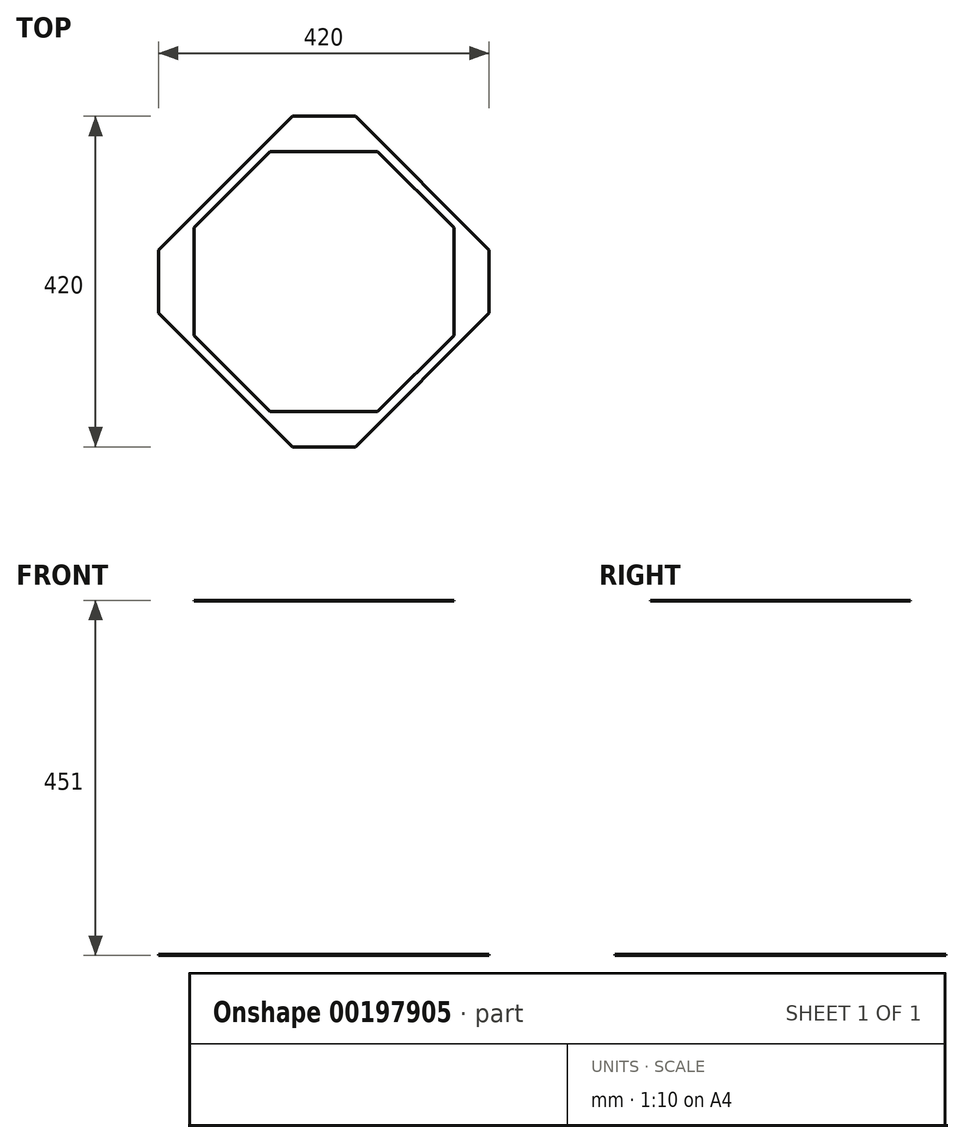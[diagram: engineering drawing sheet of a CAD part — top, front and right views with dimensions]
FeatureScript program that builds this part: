
annotation { "Feature Type Name" : "Feature", "Feature Type Description" : "" }
export const myFeature = defineFeature(function(context is Context, id is Id, definition is map)
    precondition{}
    {
        {
            var Q0;
            Q0=qCreatedBy(makeId("Top.planeOp"),FACE);
            cPlane(context, id + "F0", {"entities" : qUnion([Q0]), "cplaneType" : CPlaneType.OFFSET, "offset" : 450 * mm, "width" : 150 * mm, "height" : 150 * mm});
        }
        {
            var Q0;
            Q0=qCreatedBy(id+"F0.planeOp",FACE);
            var sketch = newSketch(context, id + "F1", { "sketchPlane" : qUnion([Q0])});
            skLineSegment(sketch, "E0", {"start": v(-268.04, 0) * mm, "end": v(272.69, 0) * mm, "construction": true});
            skLineSegment(sketch, "E1", {"start": v(0, -270.5) * mm, "end": v(0, 286.74) * mm, "construction": true});
            skLineSegment(sketch, "E2.0", {"start": v(165, 68.35) * mm, "end": v(165, -68.35) * mm});
            skLineSegment(sketch, "E2.1", {"start": v(165, -68.35) * mm, "end": v(68.35, -165) * mm});
            skLineSegment(sketch, "E2.2", {"start": v(68.35, -165) * mm, "end": v(-68.35, -165) * mm});
            skLineSegment(sketch, "E2.3", {"start": v(-68.35, -165) * mm, "end": v(-165, -68.35) * mm});
            skLineSegment(sketch, "E2.4", {"start": v(-165, -68.35) * mm, "end": v(-165, 68.35) * mm});
            skLineSegment(sketch, "E2.5", {"start": v(-165, 68.35) * mm, "end": v(-68.35, 165) * mm});
            skLineSegment(sketch, "E2.6", {"start": v(-68.35, 165) * mm, "end": v(68.35, 165) * mm});
            skLineSegment(sketch, "E2.7", {"start": v(68.35, 165) * mm, "end": v(165, 68.35) * mm});
            skPoint(sketch, "E2.0.midPoint", {"position": v(165, 0) * mm});
            skSolve(sketch);
        }
        {
            var Q0;
            Q0=qCreatedBy(makeId("Top.planeOp"),FACE);
            var sketch = newSketch(context, id + "F2", { "sketchPlane" : qUnion([Q0])});
            skLineSegment(sketch, "E3.1", {"start": v(-210, -40) * mm, "end": v(-210, 40) * mm});
            skLineSegment(sketch, "E3.2", {"start": v(-40, 210) * mm, "end": v(40, 210) * mm});
            skLineSegment(sketch, "E3.5", {"start": v(210, 40) * mm, "end": v(210, -40) * mm});
            skLineSegment(sketch, "E3.7", {"start": v(40, -210) * mm, "end": v(-40, -210) * mm});
            skSolve(sketch);
        }
        {
            var Q0;
            Q0=sQuery(id+"F2.wireOp",VERTEX,"E3.5.end");
            var Q1;
            Q1=sQuery(id+"F2.wireOp",VERTEX,"E3.5.start");
            var Q2;
            Q2=sQuery(id+"F1.wireOp",VERTEX,"E2.1.start");
            cPlane(context, id + "F3", {"entities" : qUnion([Q0, Q1, Q2]), "cplaneType" : CPlaneType.THREE_POINT, "offset" : 25 * mm, "width" : 150 * mm, "height" : 150 * mm});
        }
        {
            var Q0;
            Q0=sQuery(id+"F2.wireOp",VERTEX,"E3.5.end");
            var Q1;
            Q1=sQuery(id+"F1.wireOp",VERTEX,"E2.2.start");
            var Q2;
            Q2=sQuery(id+"F1.wireOp",VERTEX,"E2.0.end");
            cPlane(context, id + "F4", {"entities" : qUnion([Q0, Q1, Q2]), "cplaneType" : CPlaneType.THREE_POINT, "offset" : 25 * mm, "width" : 150 * mm, "height" : 150 * mm});
        }
        {
            var Q0;
            Q0=sQuery(id+"F2.wireOp",VERTEX,"E3.7.end");
            var Q1;
            Q1=sQuery(id+"F2.wireOp",VERTEX,"E3.7.start");
            var Q2;
            Q2=sQuery(id+"F1.wireOp",VERTEX,"E2.3.start");
            cPlane(context, id + "F5", {"entities" : qUnion([Q0, Q1, Q2]), "cplaneType" : CPlaneType.THREE_POINT, "offset" : 25 * mm, "width" : 150 * mm, "height" : 150 * mm});
        }
        {
            var Q0;
            Q0=sQuery(id+"F1.wireOp",VERTEX,"E2.3.start");
            var Q1;
            Q1=sQuery(id+"F1.wireOp",VERTEX,"E2.4.start");
            var Q2;
            Q2=sQuery(id+"F2.wireOp",VERTEX,"E3.7.end");
            cPlane(context, id + "F6", {"entities" : qUnion([Q0, Q1, Q2]), "cplaneType" : CPlaneType.THREE_POINT, "offset" : 25 * mm, "width" : 150 * mm, "height" : 150 * mm});
        }
        {
            var Q0;
            Q0=sQuery(id+"F2.wireOp",VERTEX,"E3.1.end");
            var Q1;
            Q1=sQuery(id+"F2.wireOp",VERTEX,"E3.1.start");
            var Q2;
            Q2=sQuery(id+"F1.wireOp",VERTEX,"E2.5.start");
            cPlane(context, id + "F7", {"entities" : qUnion([Q0, Q1, Q2]), "cplaneType" : CPlaneType.THREE_POINT, "offset" : 25 * mm, "width" : 150 * mm, "height" : 150 * mm});
        }
        {
            var Q0;
            Q0=sQuery(id+"F1.wireOp",VERTEX,"E2.6.start");
            var Q1;
            Q1=sQuery(id+"F1.wireOp",VERTEX,"E2.5.start");
            var Q2;
            Q2=sQuery(id+"F2.wireOp",VERTEX,"E3.2.start");
            cPlane(context, id + "F8", {"entities" : qUnion([Q0, Q1, Q2]), "cplaneType" : CPlaneType.THREE_POINT, "offset" : 25 * mm, "width" : 150 * mm, "height" : 150 * mm});
        }
        {
            var Q0;
            Q0=sQuery(id+"F2.wireOp",VERTEX,"E3.2.end");
            var Q1;
            Q1=sQuery(id+"F2.wireOp",VERTEX,"E3.2.start");
            var Q2;
            Q2=sQuery(id+"F1.wireOp",VERTEX,"E2.6.end");
            cPlane(context, id + "F9", {"entities" : qUnion([Q0, Q1, Q2]), "cplaneType" : CPlaneType.THREE_POINT, "offset" : 25 * mm, "width" : 150 * mm, "height" : 150 * mm});
        }
        {
            var Q0;
            Q0=sQuery(id+"F1.wireOp",VERTEX,"E2.7.end");
            var Q1;
            Q1=sQuery(id+"F1.wireOp",VERTEX,"E2.6.end");
            var Q2;
            Q2=sQuery(id+"F2.wireOp",VERTEX,"E3.5.start");
            cPlane(context, id + "F10", {"entities" : qUnion([Q0, Q1, Q2]), "cplaneType" : CPlaneType.THREE_POINT, "offset" : 25 * mm, "width" : 150 * mm, "height" : 150 * mm});
        }
        {
            var Q0;
            Q0=qCreatedBy(id+"F3.planeOp",FACE);
            var sketch = newSketch(context, id + "F11", { "sketchPlane" : qUnion([Q0])});
            skPoint(sketch, "E4.0", {"position": v(40, -20.9) * mm});
            skPoint(sketch, "E4.1", {"position": v(-40, -20.9) * mm});
            skPoint(sketch, "E5.0", {"position": v(68.35, 431.35) * mm});
            skPoint(sketch, "E6.0", {"position": v(-68.35, 431.35) * mm});
            skLineSegment(sketch, "E7", {"start": v(40, -20.9) * mm, "end": v(68.35, 431.35) * mm});
            skLineSegment(sketch, "E8", {"start": v(-68.35, 431.35) * mm, "end": v(-40, -20.9) * mm});
            skLineSegment(sketch, "E9", {"start": v(68.35, 431.35) * mm, "end": v(-40, -20.9) * mm});
            skLineSegment(sketch, "E10", {"start": v(40, -20.9) * mm, "end": v(-68.35, 431.35) * mm});
            skSolve(sketch);
        }
        {
            var Q0;
            Q0=qCreatedBy(id+"F4.planeOp",FACE);
            var sketch = newSketch(context, id + "F12", { "sketchPlane" : qUnion([Q0])});
            skPoint(sketch, "E11.0", {"position": v(-56.67, 447.16) * mm});
            skPoint(sketch, "E12.0", {"position": v(79.97, 443.59) * mm});
            skPoint(sketch, "E13.0", {"position": v(-120.29, -1.48) * mm});
            skPoint(sketch, "E14.0", {"position": v(120.05, -7.77) * mm});
            skLineSegment(sketch, "E15", {"start": v(120.05, -7.77) * mm, "end": v(-56.67, 447.16) * mm});
            skLineSegment(sketch, "E16", {"start": v(-120.29, -1.48) * mm, "end": v(79.97, 443.59) * mm});
            skSolve(sketch);
        }
        {
            var Q0;
            Q0=qCreatedBy(id+"F5.planeOp",FACE);
            var sketch = newSketch(context, id + "F13", { "sketchPlane" : qUnion([Q0])});
            skPoint(sketch, "E17.0", {"position": v(68.35, 431.35) * mm});
            skPoint(sketch, "E18.0", {"position": v(-68.35, 431.35) * mm});
            skPoint(sketch, "E19.0", {"position": v(40, -20.9) * mm});
            skPoint(sketch, "E20.0", {"position": v(-40, -20.9) * mm});
            skLineSegment(sketch, "E21", {"start": v(68.35, 431.35) * mm, "end": v(40, -20.9) * mm});
            skLineSegment(sketch, "E22", {"start": v(40, -20.9) * mm, "end": v(-68.35, 431.35) * mm});
            skLineSegment(sketch, "E23", {"start": v(-68.35, 431.35) * mm, "end": v(-40, -20.9) * mm});
            skLineSegment(sketch, "E24", {"start": v(-40, -20.9) * mm, "end": v(68.35, 431.35) * mm});
            skSolve(sketch);
        }
        {
            var Q0;
            Q0=qCreatedBy(id+"F6.planeOp",FACE);
            var sketch = newSketch(context, id + "F14", { "sketchPlane" : qUnion([Q0])});
            skPoint(sketch, "E25.0", {"position": v(79.97, 443.59) * mm});
            skPoint(sketch, "E26.0", {"position": v(-56.67, 447.16) * mm});
            skPoint(sketch, "E27.0", {"position": v(120.05, -7.77) * mm});
            skPoint(sketch, "E28.0", {"position": v(-120.29, -1.48) * mm});
            skLineSegment(sketch, "E29", {"start": v(79.97, 443.59) * mm, "end": v(-120.29, -1.48) * mm});
            skLineSegment(sketch, "E30", {"start": v(120.05, -7.77) * mm, "end": v(-56.67, 447.16) * mm});
            skSolve(sketch);
        }
        {
            var Q0;
            Q0=qCreatedBy(id+"F7.planeOp",FACE);
            var sketch = newSketch(context, id + "F15", { "sketchPlane" : qUnion([Q0])});
            skPoint(sketch, "E31.0", {"position": v(68.35, 431.35) * mm});
            skPoint(sketch, "E32.0", {"position": v(-68.35, 431.35) * mm});
            skPoint(sketch, "E33.0", {"position": v(40, -20.9) * mm});
            skPoint(sketch, "E34.0", {"position": v(-40, -20.9) * mm});
            skLineSegment(sketch, "E35", {"start": v(68.35, 431.35) * mm, "end": v(40, -20.9) * mm});
            skLineSegment(sketch, "E36", {"start": v(-68.35, 431.35) * mm, "end": v(40, -20.9) * mm});
            skLineSegment(sketch, "E37", {"start": v(-40, -20.9) * mm, "end": v(68.35, 431.35) * mm});
            skLineSegment(sketch, "E38", {"start": v(-68.35, 431.35) * mm, "end": v(-40, -20.9) * mm});
            skSolve(sketch);
        }
        {
            var Q0;
            Q0=qCreatedBy(id+"F8.planeOp",FACE);
            var sketch = newSketch(context, id + "F16", { "sketchPlane" : qUnion([Q0])});
            skPoint(sketch, "E39.0", {"position": v(-79.97, 443.59) * mm});
            skPoint(sketch, "E40.0", {"position": v(56.67, 447.16) * mm});
            skPoint(sketch, "E41.0", {"position": v(-120.05, -7.77) * mm});
            skPoint(sketch, "E42.0", {"position": v(120.29, -1.48) * mm});
            skLineSegment(sketch, "E43", {"start": v(-120.05, -7.77) * mm, "end": v(56.67, 447.16) * mm});
            skLineSegment(sketch, "E44", {"start": v(-79.97, 443.59) * mm, "end": v(120.29, -1.48) * mm});
            skSolve(sketch);
        }
        {
            var Q0;
            Q0=qCreatedBy(id+"F9.planeOp",FACE);
            var sketch = newSketch(context, id + "F17", { "sketchPlane" : qUnion([Q0])});
            skPoint(sketch, "E45.0", {"position": v(68.35, 431.35) * mm});
            skPoint(sketch, "E46.0", {"position": v(-68.35, 431.35) * mm});
            skPoint(sketch, "E47.0", {"position": v(40, -20.9) * mm});
            skPoint(sketch, "E48.0", {"position": v(-40, -20.9) * mm});
            skLineSegment(sketch, "E49", {"start": v(68.35, 431.35) * mm, "end": v(40, -20.9) * mm});
            skLineSegment(sketch, "E50", {"start": v(40, -20.9) * mm, "end": v(-68.35, 431.35) * mm});
            skLineSegment(sketch, "E51", {"start": v(-68.35, 431.35) * mm, "end": v(-40, -20.9) * mm});
            skLineSegment(sketch, "E52", {"start": v(-40, -20.9) * mm, "end": v(68.35, 431.35) * mm});
            skSolve(sketch);
        }
        {
            var Q0;
            Q0=qCreatedBy(id+"F0.planeOp",FACE);
            var sketch = newSketch(context, id + "F18", { "sketchPlane" : qUnion([Q0])});
            skLineSegment(sketch, "E53.0.0", {"start": v(165, 68.35) * mm, "end": v(68.35, 165) * mm});
            skLineSegment(sketch, "E53.0.1", {"start": v(68.35, 165) * mm, "end": v(-68.35, 165) * mm});
            skLineSegment(sketch, "E53.0.2", {"start": v(-68.35, 165) * mm, "end": v(-165, 68.35) * mm});
            skLineSegment(sketch, "E53.0.3", {"start": v(-165, 68.35) * mm, "end": v(-165, -68.35) * mm});
            skLineSegment(sketch, "E53.0.4", {"start": v(-165, -68.35) * mm, "end": v(-68.35, -165) * mm});
            skLineSegment(sketch, "E53.0.5", {"start": v(-68.35, -165) * mm, "end": v(68.35, -165) * mm});
            skLineSegment(sketch, "E53.0.6", {"start": v(68.35, -165) * mm, "end": v(165, -68.35) * mm});
            skLineSegment(sketch, "E53.0.7", {"start": v(165, -68.35) * mm, "end": v(165, 68.35) * mm});
            skLineSegment(sketch, "E54", {"start": v(68.35, -165) * mm, "end": v(-165, -68.35) * mm});
            skLineSegment(sketch, "E55", {"start": v(-165, -68.35) * mm, "end": v(-68.35, 165) * mm});
            skLineSegment(sketch, "E56", {"start": v(-68.35, 165) * mm, "end": v(165, 68.35) * mm});
            skLineSegment(sketch, "E57", {"start": v(165, 68.35) * mm, "end": v(68.35, -165) * mm});
            skLineSegment(sketch, "E58", {"start": v(-68.35, -165) * mm, "end": v(165, -68.35) * mm});
            skLineSegment(sketch, "E59", {"start": v(165, -68.35) * mm, "end": v(68.35, 165) * mm});
            skLineSegment(sketch, "E60", {"start": v(68.35, 165) * mm, "end": v(-165, 68.35) * mm});
            skLineSegment(sketch, "E61", {"start": v(-165, 68.35) * mm, "end": v(-68.35, -165) * mm});
            skLineSegment(sketch, "E62", {"start": v(68.35, -165) * mm, "end": v(-165, 68.35) * mm});
            skLineSegment(sketch, "E63", {"start": v(-165, 68.35) * mm, "end": v(165, 68.35) * mm});
            skLineSegment(sketch, "E64", {"start": v(165, 68.35) * mm, "end": v(-68.35, -165) * mm});
            skLineSegment(sketch, "E65", {"start": v(-68.35, -165) * mm, "end": v(-68.35, 165) * mm});
            skLineSegment(sketch, "E66", {"start": v(-68.35, 165) * mm, "end": v(165, -68.35) * mm});
            skLineSegment(sketch, "E67", {"start": v(165, -68.35) * mm, "end": v(-165, -68.35) * mm});
            skLineSegment(sketch, "E68", {"start": v(-165, -68.35) * mm, "end": v(68.35, 165) * mm});
            skLineSegment(sketch, "E69", {"start": v(68.35, 165) * mm, "end": v(68.35, -165) * mm});
            skLineSegment(sketch, "E70", {"start": v(68.35, -165) * mm, "end": v(-68.35, 165) * mm});
            skLineSegment(sketch, "E71", {"start": v(68.35, 165) * mm, "end": v(-68.35, -165) * mm});
            skLineSegment(sketch, "E72", {"start": v(-165, -68.35) * mm, "end": v(165, 68.35) * mm});
            skLineSegment(sketch, "E73", {"start": v(165, -68.35) * mm, "end": v(-165, 68.35) * mm});
            skSolve(sketch);
        }
        {
            var Q0;
            Q0=qCreatedBy(id+"F0.planeOp",FACE);
            var sketch = newSketch(context, id + "F19", { "sketchPlane" : qUnion([Q0])});
            skLineSegment(sketch, "E74.0", {"start": v(-165, 68.35) * mm, "end": v(-165, -68.35) * mm});
            skLineSegment(sketch, "E75.0", {"start": v(-68.35, 165) * mm, "end": v(-165, 68.35) * mm});
            skLineSegment(sketch, "E76.0", {"start": v(68.35, 165) * mm, "end": v(-68.35, 165) * mm});
            skLineSegment(sketch, "E77.0", {"start": v(165, 68.35) * mm, "end": v(68.35, 165) * mm});
            skLineSegment(sketch, "E78.0", {"start": v(165, -68.35) * mm, "end": v(165, 68.35) * mm});
            skLineSegment(sketch, "E79.0", {"start": v(68.35, -165) * mm, "end": v(165, -68.35) * mm});
            skLineSegment(sketch, "E80.0", {"start": v(-68.35, -165) * mm, "end": v(68.35, -165) * mm});
            skLineSegment(sketch, "E81.0", {"start": v(-165, -68.35) * mm, "end": v(-68.35, -165) * mm});
            skSolve(sketch);
        }
        {
            var Q0;
            Q0 = qSketchRegion(id + "F19", true);
            extrude(context, id + "F20", {"entities" : qUnion([Q0]), "depth" : 1 * mm});
        }
        {
            var Q0;
            Q0=qCreatedBy(makeId("Top.planeOp"),FACE);
            var sketch = newSketch(context, id + "F21", { "sketchPlane" : qUnion([Q0])});
            skLineSegment(sketch, "E82.0", {"start": v(-210, -40) * mm, "end": v(-210, 40) * mm});
            skLineSegment(sketch, "E83.0", {"start": v(40, -210) * mm, "end": v(-40, -210) * mm});
            skLineSegment(sketch, "E84.0", {"start": v(210, 40) * mm, "end": v(210, -40) * mm});
            skLineSegment(sketch, "E85.0", {"start": v(-40, 210) * mm, "end": v(40, 210) * mm});
            skLineSegment(sketch, "E86", {"start": v(-210, -40) * mm, "end": v(-40, -210) * mm});
            skLineSegment(sketch, "E87", {"start": v(40, -210) * mm, "end": v(210, -40) * mm});
            skLineSegment(sketch, "E88", {"start": v(210, 40) * mm, "end": v(40, 210) * mm});
            skLineSegment(sketch, "E89", {"start": v(-40, 210) * mm, "end": v(-210, 40) * mm});
            skSolve(sketch);
        }
        {
            var Q0;
            Q0 = qSketchRegion(id + "F21", true);
            extrude(context, id + "F22", {"entities" : qUnion([Q0]), "depth" : 1 * mm});
        }
    });
